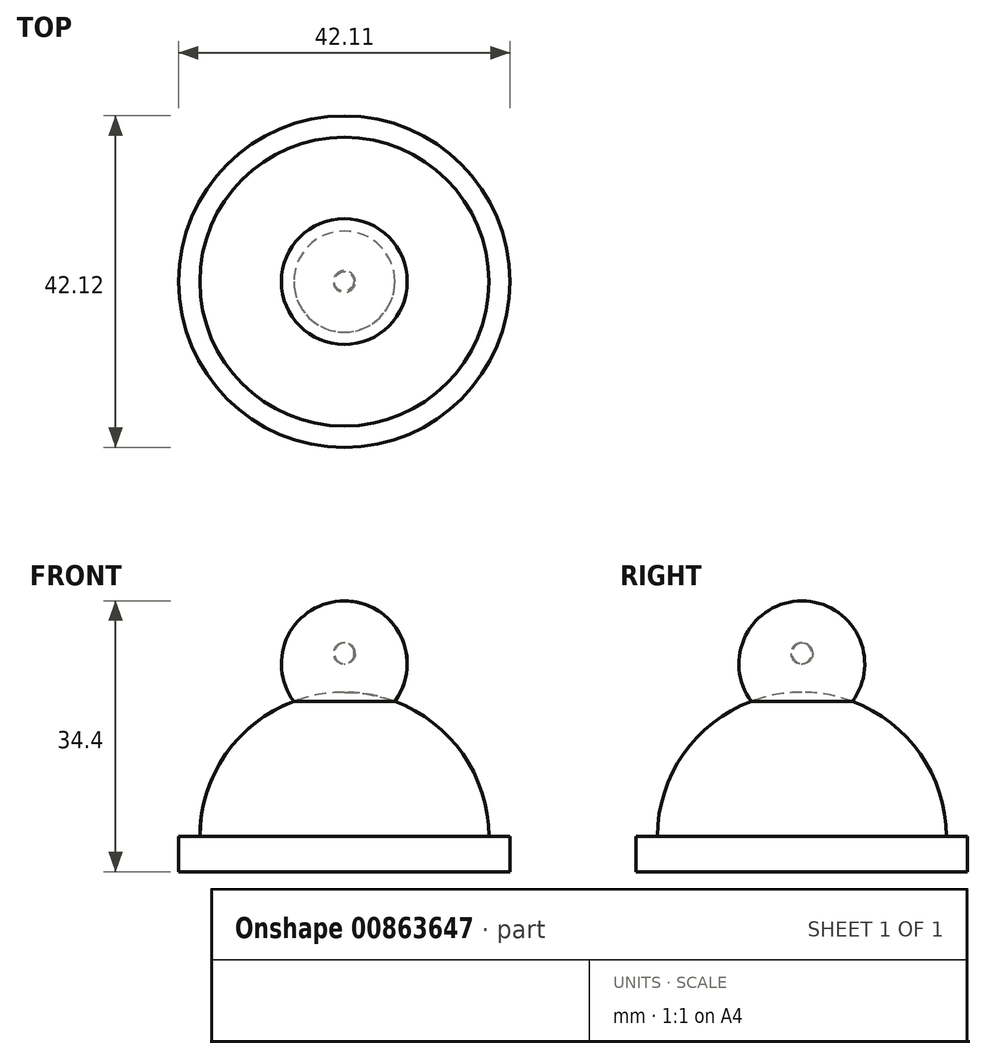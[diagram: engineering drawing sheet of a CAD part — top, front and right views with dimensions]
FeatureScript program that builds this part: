
annotation { "Feature Type Name" : "Feature", "Feature Type Description" : "" }
export const myFeature = defineFeature(function(context is Context, id is Id, definition is map)
    precondition{}
    {
        {
            var Q0;
            Q0=qCreatedBy(makeId("Front.planeOp"),FACE);
            var sketch = newSketch(context, id + "F0", { "sketchPlane" : qUnion([Q0])});
            skLineSegment(sketch, "E0", {"start": v(-21.51, -55.49) * mm, "end": v(20, -55.49) * mm});
            skLineSegment(sketch, "E1", {"start": v(20, -55.49) * mm, "end": v(20, -50.98) * mm});
            skLineSegment(sketch, "E2", {"start": v(20, -50.98) * mm, "end": v(-21.51, -50.98) * mm});
            skLineSegment(sketch, "E3", {"start": v(-21.51, -50.98) * mm, "end": v(-21.51, -55.49) * mm});
            skLineSegment(sketch, "E4", {"start": v(-21.51, -50.98) * mm, "end": v(-19.4, -50.98) * mm});
            skLineSegment(sketch, "E5", {"start": v(20, -50.98) * mm, "end": v(17.29, -50.98) * mm});
            skLineSegment(sketch, "E6", {"start": v(-19.4, -50.98) * mm, "end": v(17.29, -50.98) * mm});
            skArc(sketch, "E7", {"start": v(17.29, -50.98) * mm, "mid": v(-1.06, -32.7) * mm, "end": v(-19.4, -50.98) * mm});
            skLineSegment(sketch, "E8", {"start": v(-7.47, -33.85) * mm, "end": v(5.36, -33.85) * mm});
            skArc(sketch, "E9", {"start": v(5.36, -33.85) * mm, "mid": v(-1.06, -21.1) * mm, "end": v(-7.47, -33.85) * mm});
            skLineSegment(sketch, "E10", {"start": v(-1.06, -29.09) * mm, "end": v(-1.06, -26.43) * mm});
            skArc(sketch, "E11", {"start": v(-1.06, -29.09) * mm, "mid": v(0.2, -27.76) * mm, "end": v(-1.06, -26.43) * mm});
            skLineSegment(sketch, "E12", {"start": v(-1.06, -51.04) * mm, "end": v(-1.06, -55.49) * mm});
            skLineSegment(sketch, "E13", {"start": v(-1.06, -55.49) * mm, "end": v(-1.06, -51.04) * mm});
            skLineSegment(sketch, "E14", {"start": v(-1.06, -51.04) * mm, "end": v(-1.06, -21.1) * mm});
            skSolve(sketch);
        }
        {
            var Q0;
            Q0=qCreatedBy(makeId("Front.planeOp"),FACE);
            var sketch = newSketch(context, id + "F1", { "sketchPlane" : qUnion([Q0])});
            skSolve(sketch);
        }
        {
            var Q0;
            {var subQ4=sQuery(id+"F0.wireOp",EDGE,"E1");Q0=makeQuery(id+"F0.imprint","IMPRINT",FACE,{"disambiguationData":[TD([[makeQuery(id+"F0.imprint","IMPRINT",EDGE,{"derivedFrom":subQ4}),1.0]])]});}
            var Q1;
            {var subQ1=sQuery(id+"F0.wireOp",EDGE,"E11");Q1=makeQuery(id+"F0.imprint","IMPRINT",FACE,{"disambiguationData":[TD([[makeQuery(id+"F0.imprint","IMPRINT",EDGE,{"derivedFrom":subQ1}),-1.0]])]});}
            var Q2;
            {var subQ0=sQuery(id+"F0.wireOp",EDGE,"E7");var subQ1=sQuery(id+"F0.wireOp",EDGE,"E2");var subQ2=makeQuery(id+"F0.imprint","INTERSECT",VERTEX,{"disambiguationData":[OD(0.0)],"derivedFrom":[subQ1,subQ0]});Q2=makeQuery(id+"F0.imprint","IMPRINT",FACE,{"disambiguationData":[TD([[makeQuery(id+"F0.imprint","IMPRINT",EDGE,{"disambiguationData":[TD([[subQ2,-1.0]])],"derivedFrom":subQ1}),-1.0]])]});}
            var Q3;
            Q3=sQuery(id+"F0.wireOp",EDGE,"E14");
            revolve(context, id + "F2", {"surfaceOperationType" : NewSurfaceOperationType.NEW, "entities" : qUnion([Q0, Q1, Q2]), "axis" : qUnion([Q3]), "revolveType" : RevolveType.FULL});
        }
    });
